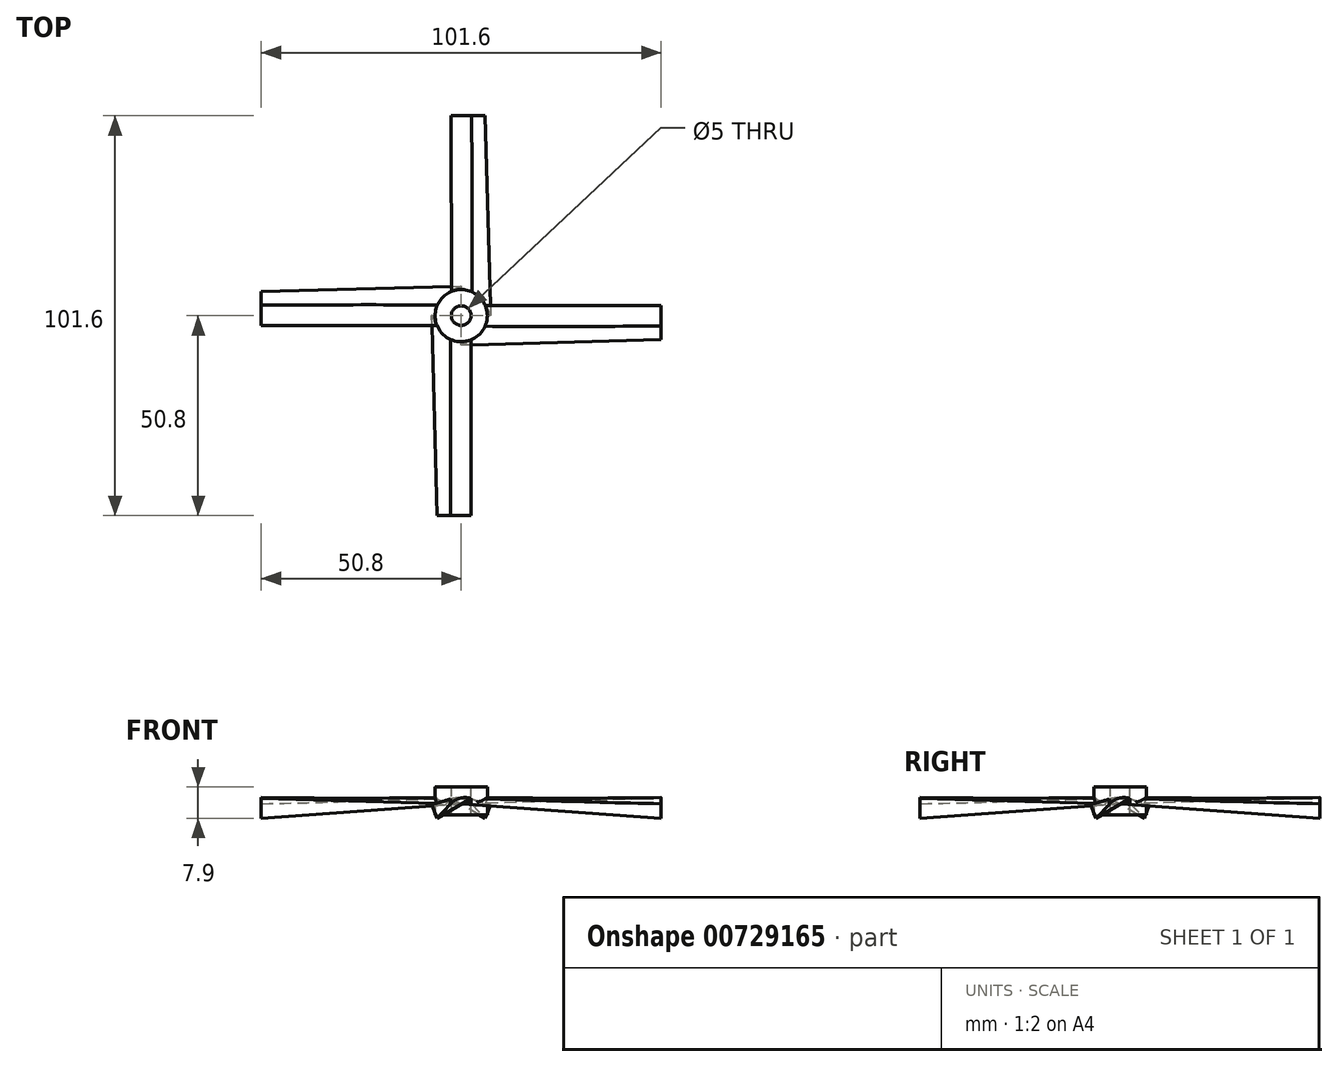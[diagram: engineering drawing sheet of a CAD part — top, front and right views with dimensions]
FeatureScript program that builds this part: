
annotation { "Feature Type Name" : "Feature", "Feature Type Description" : "" }
export const myFeature = defineFeature(function(context is Context, id is Id, definition is map)
    precondition{}
    {
        {
            var Q0;
            Q0=qCreatedBy(makeId("Front.planeOp"),FACE);
            var sketch = newSketch(context, id + "F0", { "sketchPlane" : qUnion([Q0])});
            skLineSegment(sketch, "E0", {"start": v(-50.8, 0) * mm, "end": v(50.8, 0) * mm, "construction": true});
            skLineSegment(sketch, "E1", {"start": v(0, 0) * mm, "end": v(0, 21.4) * mm, "construction": true});
            skSolve(sketch);
        }
        {
            var Q0;
            Q0=qCreatedBy(makeId("Right.planeOp"),FACE);
            var sketch = newSketch(context, id + "F1", { "sketchPlane" : qUnion([Q0])});
            skLineSegment(sketch, "E2", {"start": v(7.5, -0.75) * mm, "end": v(-2.5, -0.75) * mm});
            skLineSegment(sketch, "E3", {"start": v(-2.5, -0.75) * mm, "end": v(-2.5, 2.25) * mm});
            skLineSegment(sketch, "E4", {"start": v(-2.5, 2.25) * mm, "end": v(7.5, -0.75) * mm});
            skLineSegment(sketch, "E5", {"start": v(-2.5, -0.75) * mm, "end": v(2.5, 0.75) * mm, "construction": true});
            skSolve(sketch);
        }
        {
            var Q0;
            Q0=sQuery(id+"F0.wireOp",VERTEX,"E0.start");
            var Q1;
            Q1=sQuery(id+"F0.wireOp",EDGE,"E0");
            cPlane(context, id + "F2", {"entities" : qUnion([Q0, Q1]), "cplaneType" : CPlaneType.LINE_POINT, "offset" : 25 * mm, "width" : 150 * mm, "height" : 150 * mm});
        }
        {
            var Q0;
            Q0=qCreatedBy(id+"F2.planeOp",FACE);
            var sketch = newSketch(context, id + "F3", { "sketchPlane" : qUnion([Q0])});
            skLineSegment(sketch, "E6.0", {"start": v(-2.5, -0.75) * mm, "end": v(2.5, 0.75) * mm, "construction": true});
            skLineSegment(sketch, "E6.1", {"start": v(-2.5, 2.25) * mm, "end": v(7.5, -0.75) * mm, "construction": true});
            skLineSegment(sketch, "E6.2", {"start": v(-2.5, -0.75) * mm, "end": v(-2.5, 2.25) * mm, "construction": true});
            skLineSegment(sketch, "E6.3", {"start": v(7.5, -0.75) * mm, "end": v(-2.5, -0.75) * mm, "construction": true});
            skLineSegment(sketch, "E7", {"start": v(6.12, -4.4) * mm, "end": v(-2.54, 0.6) * mm});
            skLineSegment(sketch, "E8", {"start": v(-2.54, 0.6) * mm, "end": v(-1.04, 3.2) * mm});
            skLineSegment(sketch, "E9", {"start": v(-1.04, 3.2) * mm, "end": v(6.12, -4.4) * mm});
            skLineSegment(sketch, "E10", {"start": v(2.54, -0.6) * mm, "end": v(-2.54, 0.6) * mm, "construction": true});
            skSolve(sketch);
        }
        {
            var Q0;
            Q0=makeQuery(id+"F3.imprint","IMPRINT",FACE,{"disambiguationData":[TD([[makeQuery(id+"F3.imprint","IMPRINT",EDGE,{"derivedFrom":sQuery(id+"F3.wireOp",EDGE,"E7")}),-1.0]])]});
            var Q1;
            Q1=makeQuery(id+"F1.imprint","IMPRINT",FACE,{"disambiguationData":[TD([[makeQuery(id+"F1.imprint","IMPRINT",EDGE,{"derivedFrom":sQuery(id+"F1.wireOp",EDGE,"E2")}),-1.0]])]});
            loft(context, id + "F4", {"sheetProfilesArray" : [{ "sheetProfileEntities" : qUnion([Q0]) }, { "sheetProfileEntities" : qUnion([Q1]) }]});
        }
        {
            var Q0;
            Q0=makeQuery(id+"F4.opLoft","SWEPT_BODY",BODY,{"disambiguationData":[OSD([makeQuery(id+"F1.imprint","IMPRINT",FACE,{"disambiguationData":[TD([[makeQuery(id+"F1.imprint","IMPRINT",EDGE,{"derivedFrom":sQuery(id+"F1.wireOp",EDGE,"E2")}),-1.0]])]}),makeQuery(id+"F3.imprint","IMPRINT",FACE,{"disambiguationData":[TD([[makeQuery(id+"F3.imprint","IMPRINT",EDGE,{"derivedFrom":sQuery(id+"F3.wireOp",EDGE,"E7")}),-1.0]])]})])]});
            var Q1;
            Q1=sQuery(id+"F0.wireOp",EDGE,"E1");
            circularPattern(context, id + "F5", {"entities" : qUnion([Q0]), "axis" : qUnion([Q1]), "angle" : 360 * degree, "instanceCount" : 4, "equalSpace" : true});
        }
        {
            var Q0;
            Q0=qCreatedBy(makeId("Top.planeOp"),FACE);
            var sketch = newSketch(context, id + "F6", { "sketchPlane" : qUnion([Q0])});
            skCircle(sketch, "E11", {"center": v(0, 0) * mm, "radius": 6.62 * mm});
            skSolve(sketch);
        }
        {
            var Q0;
            Q0=makeQuery(id+"F6.imprint","IMPRINT",FACE,{"disambiguationData":[TD([[makeQuery(id+"F6.imprint","IMPRINT",EDGE,{"derivedFrom":sQuery(id+"F6.wireOp",EDGE,"E11")}),1.0]])]});
            extrude(context, id + "F7", {"entities" : qUnion([Q0]), "operationType" : NewBodyOperationType.ADD, "endBound" : BoundingType.SYMMETRIC, "depth" : 7 * mm, "offsetDistance" : 25 * mm});
        }
        {
            var Q0;
            Q0=qCreatedBy(makeId("Top.planeOp"),FACE);
            var sketch = newSketch(context, id + "F8", { "sketchPlane" : qUnion([Q0])});
            skCircle(sketch, "E12", {"center": v(0, 0) * mm, "radius": 2.5 * mm});
            skSolve(sketch);
        }
        {
            var Q0;
            Q0 = qSketchRegion(id + "F8", true);
            extrude(context, id + "F9", {"entities" : qUnion([Q0]), "operationType" : NewBodyOperationType.REMOVE, "endBound" : BoundingType.THROUGH_ALL, "oppositeDirection" : true, "depth" : 25 * mm, "offsetDistance" : 25 * mm, "hasSecondDirection" : true, "secondDirectionBound" : SecondDirectionBoundingType.THROUGH_ALL, "secondDirectionOppositeDirection" : false, "secondDirectionDepth" : 25 * mm});
        }
        {
            var Q0;
            Q0=makeQuery(id+"F4.opLoft","SWEPT_EDGE",EDGE,{"disambiguationData":[OSD([sQuery(id+"F1.wireOp",EDGE,"E3"),sQuery(id+"F1.wireOp",EDGE,"E4"),sQuery(id+"F3.wireOp",EDGE,"E8"),sQuery(id+"F3.wireOp",EDGE,"E9")])]});
            var Q1;
            Q1=makeQuery(id+"F5.opPattern","COPY",EDGE,{"derivedFrom":makeQuery(id+"F4.opLoft","SWEPT_EDGE",EDGE,{"disambiguationData":[OSD([sQuery(id+"F1.wireOp",EDGE,"E3"),sQuery(id+"F1.wireOp",EDGE,"E4"),sQuery(id+"F3.wireOp",EDGE,"E8"),sQuery(id+"F3.wireOp",EDGE,"E9")])]}),"instanceName":"1"});
            var Q2;
            Q2=makeQuery(id+"F5.opPattern","COPY",EDGE,{"derivedFrom":makeQuery(id+"F4.opLoft","SWEPT_EDGE",EDGE,{"disambiguationData":[OSD([sQuery(id+"F1.wireOp",EDGE,"E3"),sQuery(id+"F1.wireOp",EDGE,"E4"),sQuery(id+"F3.wireOp",EDGE,"E8"),sQuery(id+"F3.wireOp",EDGE,"E9")])]}),"instanceName":"2"});
            var Q3;
            Q3=makeQuery(id+"F5.opPattern","COPY",EDGE,{"derivedFrom":makeQuery(id+"F4.opLoft","SWEPT_EDGE",EDGE,{"disambiguationData":[OSD([sQuery(id+"F1.wireOp",EDGE,"E3"),sQuery(id+"F1.wireOp",EDGE,"E4"),sQuery(id+"F3.wireOp",EDGE,"E8"),sQuery(id+"F3.wireOp",EDGE,"E9")])]}),"instanceName":"3"});
            fillet(context, id + "F10", {"entities" : qUnion([Q0, Q1, Q2, Q3]), "radius" : 5 * mm, "tangentPropagation" : true, "allowEdgeOverflow" : false});
        }
    });
